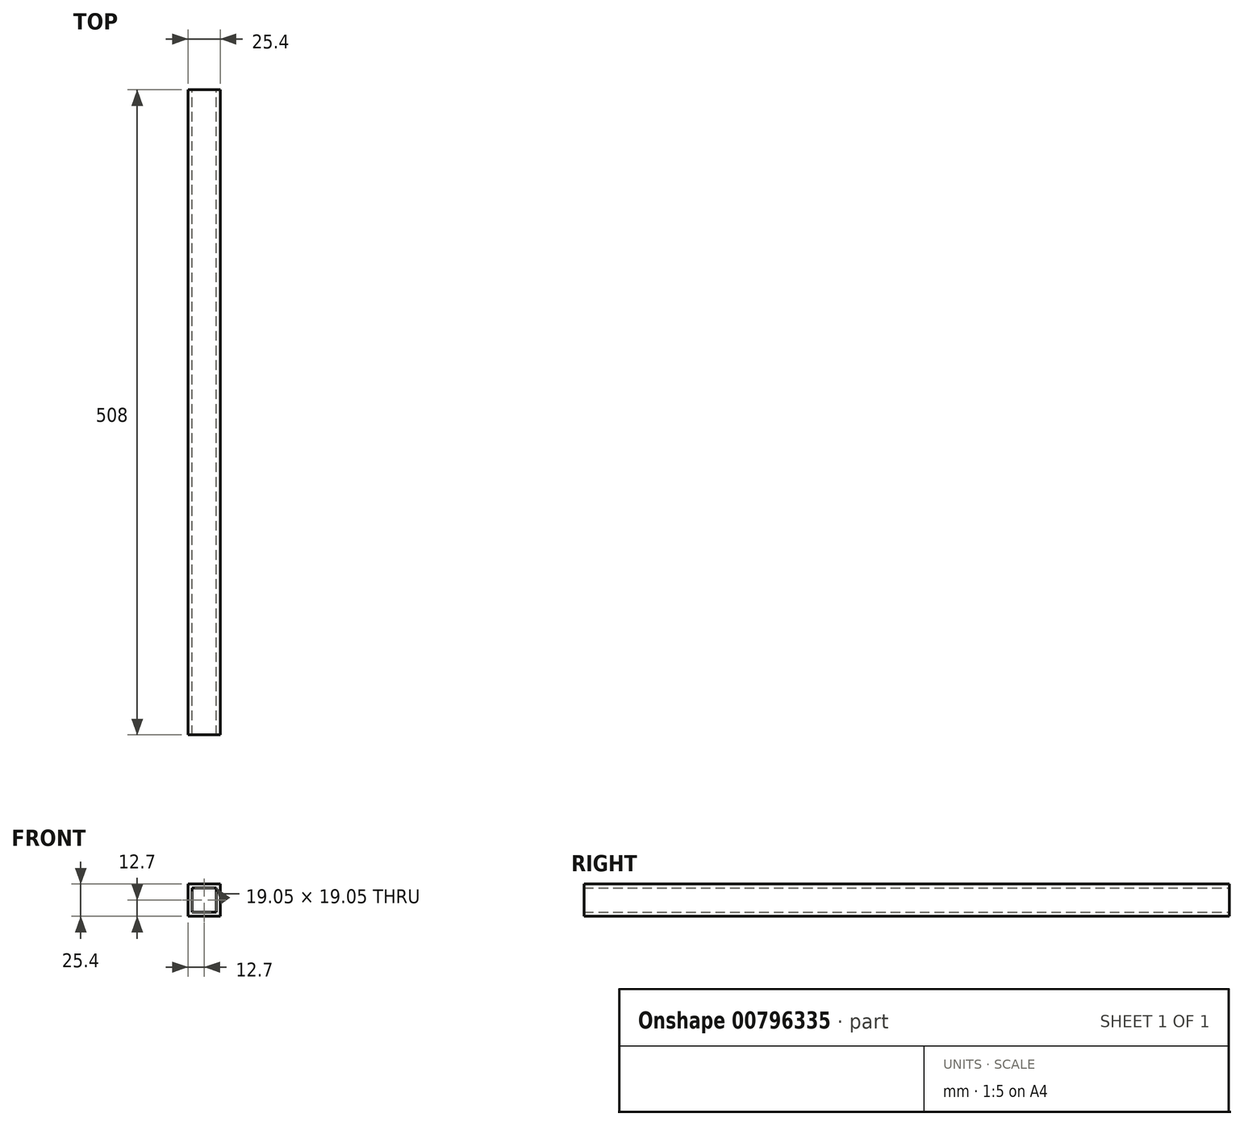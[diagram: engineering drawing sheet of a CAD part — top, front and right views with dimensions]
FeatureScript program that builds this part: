
annotation { "Feature Type Name" : "Feature", "Feature Type Description" : "" }
export const myFeature = defineFeature(function(context is Context, id is Id, definition is map)
    precondition{}
    {
        {
            var Q0;
            Q0=qCreatedBy(makeId("Front.planeOp"),FACE);
            var sketch = newSketch(context, id + "F0", { "sketchPlane" : qUnion([Q0])});
            skLineSegment(sketch, "E0.bottom", {"start": v(-12.7, 12.7) * mm, "end": v(12.7, 12.7) * mm});
            skLineSegment(sketch, "E0.top", {"start": v(-12.7, -12.7) * mm, "end": v(12.7, -12.7) * mm});
            skLineSegment(sketch, "E0.left", {"start": v(-12.7, 12.7) * mm, "end": v(-12.7, -12.7) * mm});
            skLineSegment(sketch, "E0.right", {"start": v(12.7, 12.7) * mm, "end": v(12.7, -12.7) * mm});
            skPoint(sketch, "E0.middle", {"position": v(0, 0) * mm});
            skLineSegment(sketch, "E1.bottom", {"start": v(-9.53, 9.53) * mm, "end": v(9.53, 9.53) * mm});
            skLineSegment(sketch, "E1.top", {"start": v(-9.53, -9.53) * mm, "end": v(9.53, -9.53) * mm});
            skLineSegment(sketch, "E1.left", {"start": v(-9.53, 9.53) * mm, "end": v(-9.53, -9.53) * mm});
            skLineSegment(sketch, "E1.right", {"start": v(9.53, 9.53) * mm, "end": v(9.52, -9.53) * mm});
            skSolve(sketch);
        }
        {
            var Q0;
            Q0=makeQuery(id+"F0.imprint","IMPRINT",FACE,{"disambiguationData":[TD([[makeQuery(id+"F0.imprint","IMPRINT",EDGE,{"derivedFrom":sQuery(id+"F0.wireOp",EDGE,"E0.bottom")}),-1.0]])]});
            extrude(context, id + "F1", {"entities" : qUnion([Q0]), "depth" : 508 * mm, "offsetDistance" : 25.4 * mm});
        }
    });
